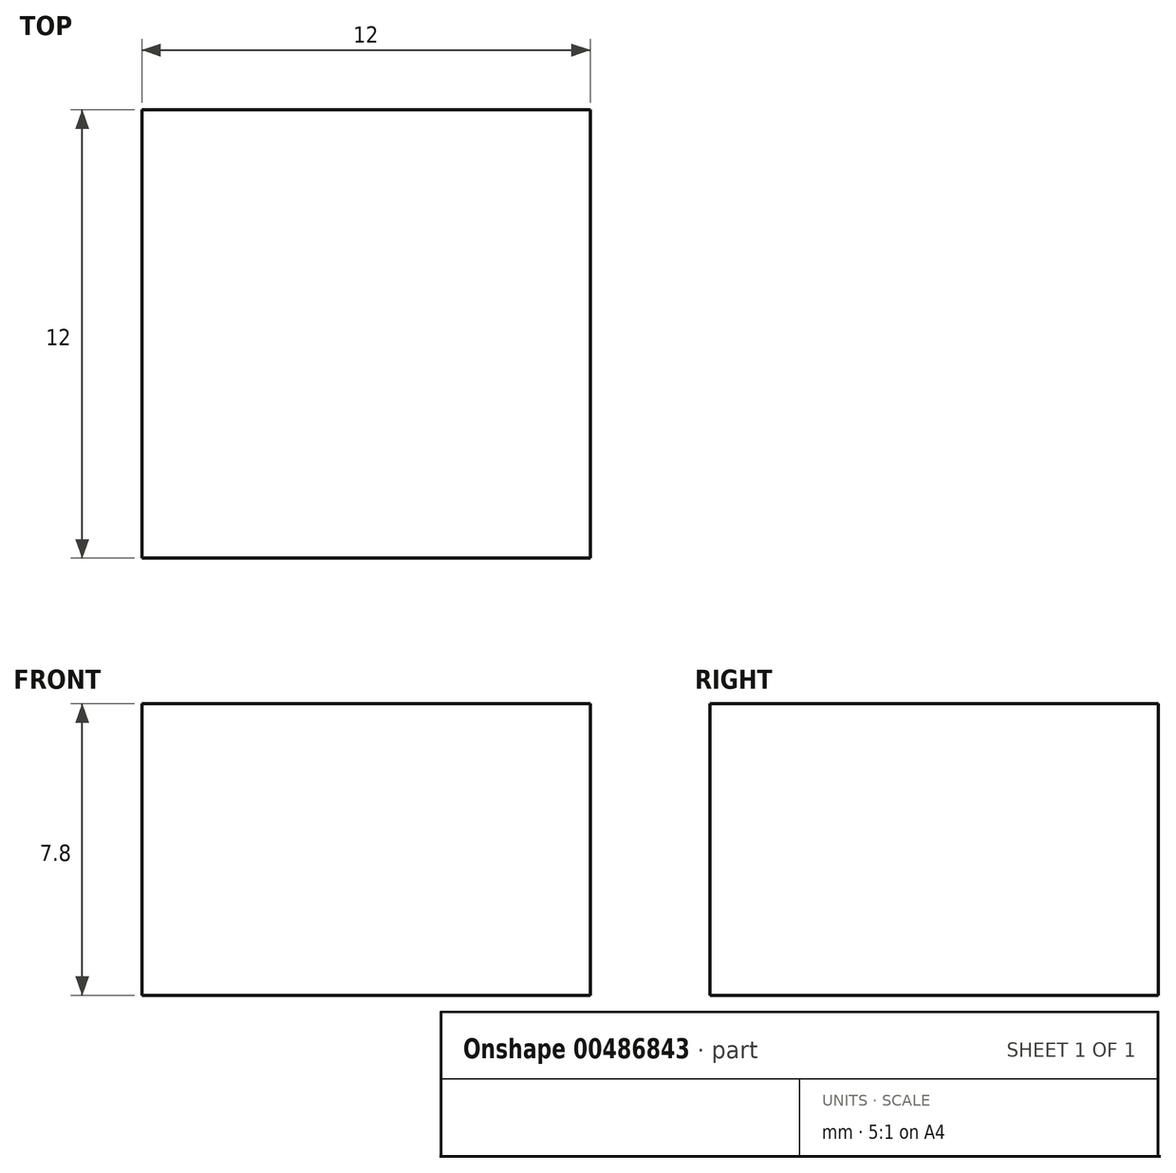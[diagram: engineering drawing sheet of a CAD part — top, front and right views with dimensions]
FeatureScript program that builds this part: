
annotation { "Feature Type Name" : "Feature", "Feature Type Description" : "" }
export const myFeature = defineFeature(function(context is Context, id is Id, definition is map)
    precondition{}
    {
        {
            var Q0;
            Q0=qCreatedBy(makeId("Top.planeOp"),FACE);
            var sketch = newSketch(context, id + "F0", { "sketchPlane" : qUnion([Q0])});
            skLineSegment(sketch, "E0.bottom", {"start": v(-8.55, 5.18) * mm, "end": v(3.45, 5.18) * mm});
            skLineSegment(sketch, "E0.top", {"start": v(-8.55, -6.82) * mm, "end": v(3.45, -6.82) * mm});
            skLineSegment(sketch, "E0.left", {"start": v(-8.55, 5.18) * mm, "end": v(-8.55, -6.82) * mm});
            skLineSegment(sketch, "E0.right", {"start": v(3.45, 5.18) * mm, "end": v(3.45, -6.82) * mm});
            skSolve(sketch);
        }
        {
            var Q0;
            Q0 = qSketchRegion(id + "F0", true);
            extrude(context, id + "F1", {"entities" : qUnion([Q0]), "depth" : 7.8 * mm});
        }
    });
